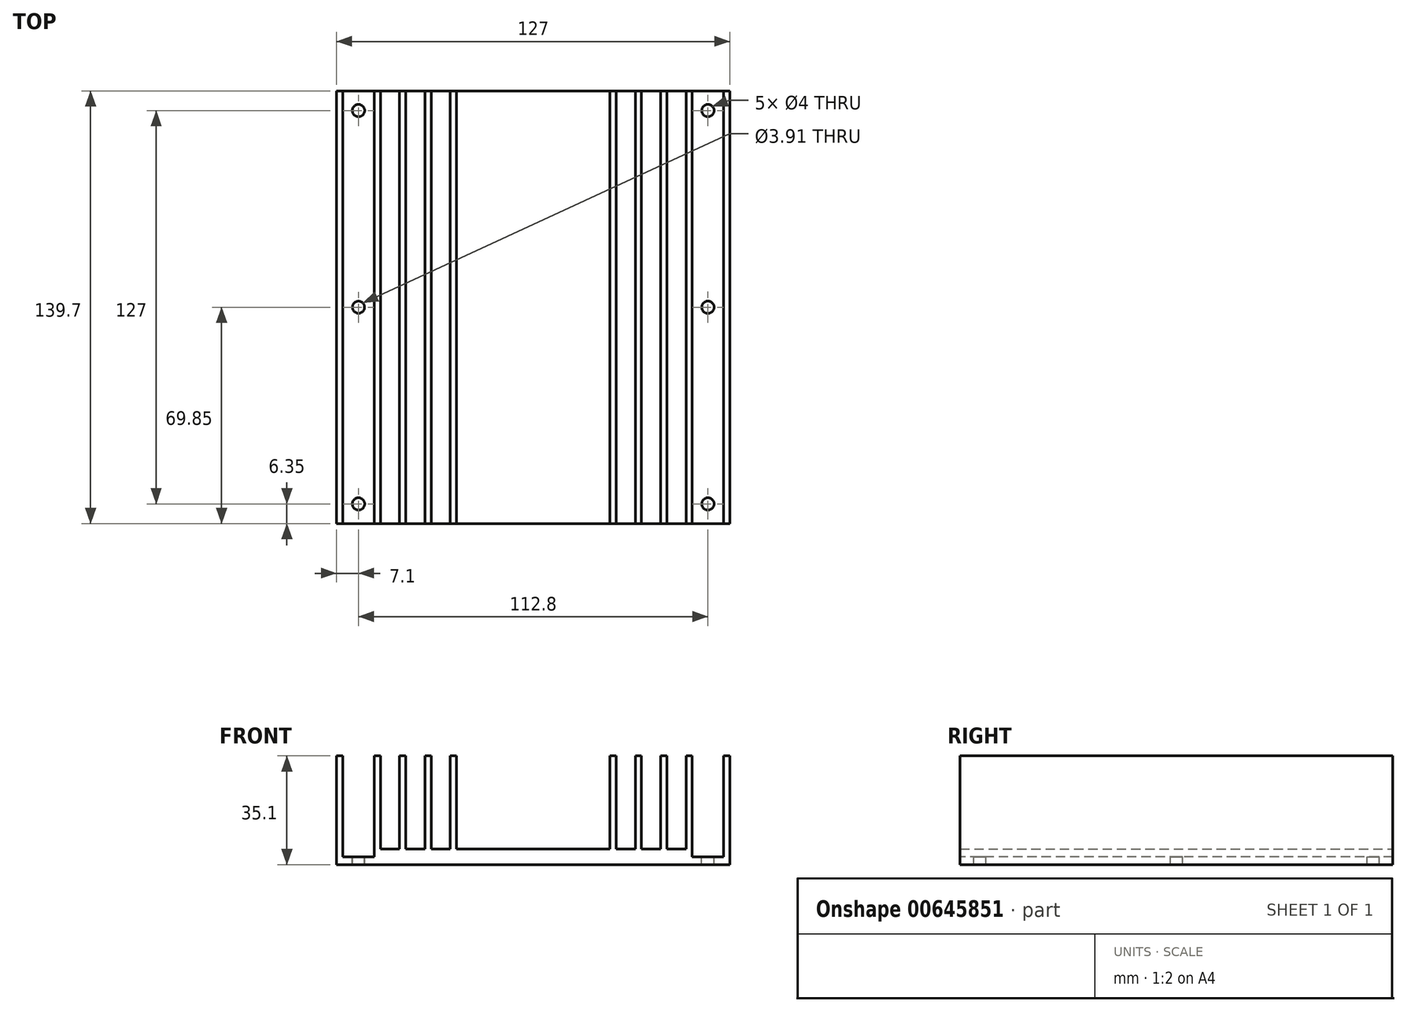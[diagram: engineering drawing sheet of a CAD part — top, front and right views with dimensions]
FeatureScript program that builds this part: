
annotation { "Feature Type Name" : "Feature", "Feature Type Description" : "" }
export const myFeature = defineFeature(function(context is Context, id is Id, definition is map)
    precondition{}
    {
        {
            var Q0;
            Q0=qCreatedBy(makeId("Front.planeOp"),FACE);
            var sketch = newSketch(context, id + "F0", { "sketchPlane" : qUnion([Q0])});
            skLineSegment(sketch, "E0.bottom", {"start": v(-63.5, 35.1) * mm, "end": v(63.5, 35.1) * mm});
            skLineSegment(sketch, "E0.top", {"start": v(-63.5, 0) * mm, "end": v(63.5, 0) * mm});
            skLineSegment(sketch, "E0.left", {"start": v(-63.5, 35.1) * mm, "end": v(-63.5, 0) * mm});
            skLineSegment(sketch, "E0.right", {"start": v(63.5, 35.1) * mm, "end": v(63.5, 0) * mm});
            skLineSegment(sketch, "E1.bottom", {"start": v(-24.75, 35.1) * mm, "end": v(24.75, 35.1) * mm});
            skLineSegment(sketch, "E1.top", {"start": v(-24.75, 5) * mm, "end": v(24.75, 5) * mm});
            skLineSegment(sketch, "E1.left", {"start": v(-24.75, 35.1) * mm, "end": v(-24.75, 5) * mm});
            skLineSegment(sketch, "E1.right", {"start": v(24.75, 35.1) * mm, "end": v(24.75, 5) * mm});
            skSolve(sketch);
        }
        {
            var Q0;
            Q0=makeQuery(id+"F0.imprint","IMPRINT",FACE,{"disambiguationData":[TD([[makeQuery(id+"F0.imprint","IMPRINT",EDGE,{"derivedFrom":sQuery(id+"F0.wireOp",EDGE,"E0.top")}),1.0]])]});
            extrude(context, id + "F1", {"entities" : qUnion([Q0]), "depth" : 139.7 * mm, "offsetDistance" : 25 * mm});
        }
        {
            var Q0;
            Q0=makeQuery(id+"F1.opExtrude","CAP_FACE",FACE,{"disambiguationData":[OSD([sQuery(id+"F0.wireOp",EDGE,"E0.bottom"),sQuery(id+"F0.wireOp",EDGE,"E0.top"),sQuery(id+"F0.wireOp",EDGE,"E0.left"),sQuery(id+"F0.wireOp",EDGE,"E0.right"),sQuery(id+"F0.wireOp",EDGE,"E1.top"),sQuery(id+"F0.wireOp",EDGE,"E1.left"),sQuery(id+"F0.wireOp",EDGE,"E1.right")])],"isStart":false});
            var sketch = newSketch(context, id + "F2", { "sketchPlane" : qUnion([Q0])});
            skLineSegment(sketch, "E2.bottom", {"start": v(-61.5, 35.1) * mm, "end": v(-51.3, 35.1) * mm});
            skLineSegment(sketch, "E2.top", {"start": v(-61.5, 2.5) * mm, "end": v(-51.3, 2.5) * mm});
            skLineSegment(sketch, "E2.left", {"start": v(-61.5, 35.1) * mm, "end": v(-61.5, 2.5) * mm});
            skLineSegment(sketch, "E2.right", {"start": v(-51.3, 35.1) * mm, "end": v(-51.3, 2.5) * mm});
            skLineSegment(sketch, "E3.bottom", {"start": v(51.3, 35.1) * mm, "end": v(61.5, 35.1) * mm});
            skLineSegment(sketch, "E3.top", {"start": v(51.3, 2.5) * mm, "end": v(61.5, 2.5) * mm});
            skLineSegment(sketch, "E3.left", {"start": v(51.3, 35.1) * mm, "end": v(51.3, 2.5) * mm});
            skLineSegment(sketch, "E3.right", {"start": v(61.5, 35.1) * mm, "end": v(61.5, 2.5) * mm});
            skSolve(sketch);
        }
        {
            var Q0;
            Q0 = qSketchRegion(id + "F2", true);
            extrude(context, id + "F3", {"entities" : qUnion([Q0]), "operationType" : NewBodyOperationType.REMOVE, "oppositeDirection" : true, "depth" : 150 * mm, "offsetDistance" : 25 * mm});
        }
        {
            var Q0;
            Q0=qCreatedBy(makeId("Front.planeOp"),FACE);
            var sketch = newSketch(context, id + "F4", { "sketchPlane" : qUnion([Q0])});
            skLineSegment(sketch, "E4.bottom", {"start": v(-32.95, 37.65) * mm, "end": v(-26.75, 37.65) * mm});
            skLineSegment(sketch, "E4.top", {"start": v(-32.95, 5) * mm, "end": v(-26.75, 5) * mm});
            skLineSegment(sketch, "E4.left", {"start": v(-32.95, 37.65) * mm, "end": v(-32.95, 5) * mm});
            skLineSegment(sketch, "E4.right", {"start": v(-26.75, 37.65) * mm, "end": v(-26.75, 5) * mm});
            skLineSegment(sketch, "E5.bottom", {"start": v(-34.95, 5) * mm, "end": v(-41.15, 5) * mm});
            skLineSegment(sketch, "E5.top", {"start": v(-34.95, 37.91) * mm, "end": v(-41.15, 37.91) * mm});
            skLineSegment(sketch, "E5.left", {"start": v(-34.95, 5) * mm, "end": v(-34.95, 37.91) * mm});
            skLineSegment(sketch, "E5.right", {"start": v(-41.15, 5) * mm, "end": v(-41.15, 37.91) * mm});
            skLineSegment(sketch, "E6.bottom", {"start": v(-43.15, 5) * mm, "end": v(-49.35, 5) * mm});
            skLineSegment(sketch, "E6.top", {"start": v(-43.15, 39.58) * mm, "end": v(-49.35, 39.58) * mm});
            skLineSegment(sketch, "E6.left", {"start": v(-43.15, 5) * mm, "end": v(-43.15, 39.58) * mm});
            skLineSegment(sketch, "E6.right", {"start": v(-49.35, 5) * mm, "end": v(-49.35, 39.58) * mm});
            skLineSegment(sketch, "E7.bottom", {"start": v(26.75, 5) * mm, "end": v(32.95, 5) * mm});
            skLineSegment(sketch, "E7.top", {"start": v(26.75, 40.14) * mm, "end": v(32.95, 40.14) * mm});
            skLineSegment(sketch, "E7.left", {"start": v(26.75, 5) * mm, "end": v(26.75, 40.14) * mm});
            skLineSegment(sketch, "E7.right", {"start": v(32.95, 5) * mm, "end": v(32.95, 40.14) * mm});
            skLineSegment(sketch, "E8.bottom", {"start": v(34.95, 5) * mm, "end": v(41.15, 5) * mm});
            skLineSegment(sketch, "E8.top", {"start": v(34.95, 40.98) * mm, "end": v(41.15, 40.98) * mm});
            skLineSegment(sketch, "E8.left", {"start": v(34.95, 5) * mm, "end": v(34.95, 40.98) * mm});
            skLineSegment(sketch, "E8.right", {"start": v(41.15, 5) * mm, "end": v(41.15, 40.98) * mm});
            skLineSegment(sketch, "E9.bottom", {"start": v(43.15, 5) * mm, "end": v(49.35, 5) * mm});
            skLineSegment(sketch, "E9.top", {"start": v(43.15, 45.16) * mm, "end": v(49.35, 45.16) * mm});
            skLineSegment(sketch, "E9.left", {"start": v(43.15, 5) * mm, "end": v(43.15, 45.16) * mm});
            skLineSegment(sketch, "E9.right", {"start": v(49.35, 5) * mm, "end": v(49.35, 45.16) * mm});
            skSolve(sketch);
        }
        {
            var Q0;
            Q0 = qSketchRegion(id + "F4", true);
            extrude(context, id + "F5", {"entities" : qUnion([Q0]), "operationType" : NewBodyOperationType.REMOVE, "oppositeDirection" : true, "depth" : 150 * mm, "offsetDistance" : 25 * mm});
        }
        {
            var Q0;
            Q0 = qSketchRegion(id + "F4", true);
            extrude(context, id + "F6", {"entities" : qUnion([Q0]), "operationType" : NewBodyOperationType.REMOVE, "depth" : 150 * mm, "offsetDistance" : 25 * mm});
        }
        {
            var Q0;
            Q0=makeQuery(id+"F3.boolean.opBoolean","COPY",FACE,{"derivedFrom":makeQuery(id+"F3.opExtrude","SWEPT_FACE",FACE,{"disambiguationData":[OSD([sQuery(id+"F2.wireOp",EDGE,"E2.top")])]})});
            var sketch = newSketch(context, id + "F7", { "sketchPlane" : qUnion([Q0])});
            skCircle(sketch, "E10", {"center": v(-56.4, -6.35) * mm, "radius": 2 * mm});
            skCircle(sketch, "E11", {"center": v(56.4, -6.35) * mm, "radius": 2 * mm});
            skCircle(sketch, "E12", {"center": v(-56.4, -69.85) * mm, "radius": 1.96 * mm});
            skCircle(sketch, "E13", {"center": v(56.4, -69.85) * mm, "radius": 2 * mm});
            skCircle(sketch, "E14", {"center": v(-56.4, -133.35) * mm, "radius": 2 * mm});
            skCircle(sketch, "E15", {"center": v(56.4, -133.35) * mm, "radius": 2 * mm});
            skSolve(sketch);
        }
        {
            var Q0;
            Q0 = qSketchRegion(id + "F7", true);
            extrude(context, id + "F8", {"entities" : qUnion([Q0]), "operationType" : NewBodyOperationType.REMOVE, "oppositeDirection" : true, "depth" : 25 * mm, "offsetDistance" : 25 * mm});
        }
    });
